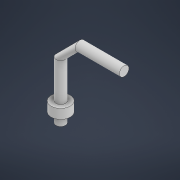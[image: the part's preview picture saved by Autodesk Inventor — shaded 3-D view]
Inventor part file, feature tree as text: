
AUTODESK INVENTOR PART (.ipt)
format: ipt  version: 2021 (Build 250183000, 183)  size: 147,968 bytes
history: native  units: mm
features: extrude x5, sketch x5, other x2, plane x1, loft x1
ambient origin geometry x8: Origin, YZ Plane, XZ Plane, XY Plane, X Axis, Y Axis, Z Axis, Center Point
bodies: Solid1 (feature_tree)
feature tree (14):
  extrude  "Extrusion1"  Depth=5.0mm TaperAngle=0.0deg
  extrude  "Extrusion2"  Depth=5.0mm TaperAngle=0.0deg
  extrude  "Extrusion3"  Depth=20.0mm TaperAngle=0.0deg
  plane  "Work Plane1"
  extrude  "Extrusion6"  Depth=15.064mm
  loft  "Loft3"
  extrude  "Extrusion7"  Depth=25.0mm TaperAngle=0.0deg
  sketch  "Sketch1"  dims[d0=10.0mm d1=5.0mm d2=0.0mm]
  sketch  "Sketch2"  dims[d3=5.0mm d4=5.0mm d5=0.0mm]
  sketch  "Sketch3"  dims[d6=5.0mm d7=20.0mm d8=0.0mm]
  sketch  "Sketch6"  dims[d9=15.0mm d28=15.064mm]
  other  "Edges5"
  other  "Edges6"
  sketch  "Sketch7"  dims[d29=4.909mm d30=5.0mm d31=25.0mm d32=0.0mm d33=0.0mm d34=90.0deg d35=0.0mm d36=90.0deg d37=5.0mm d38=1.733mm d39=0.0mm]
